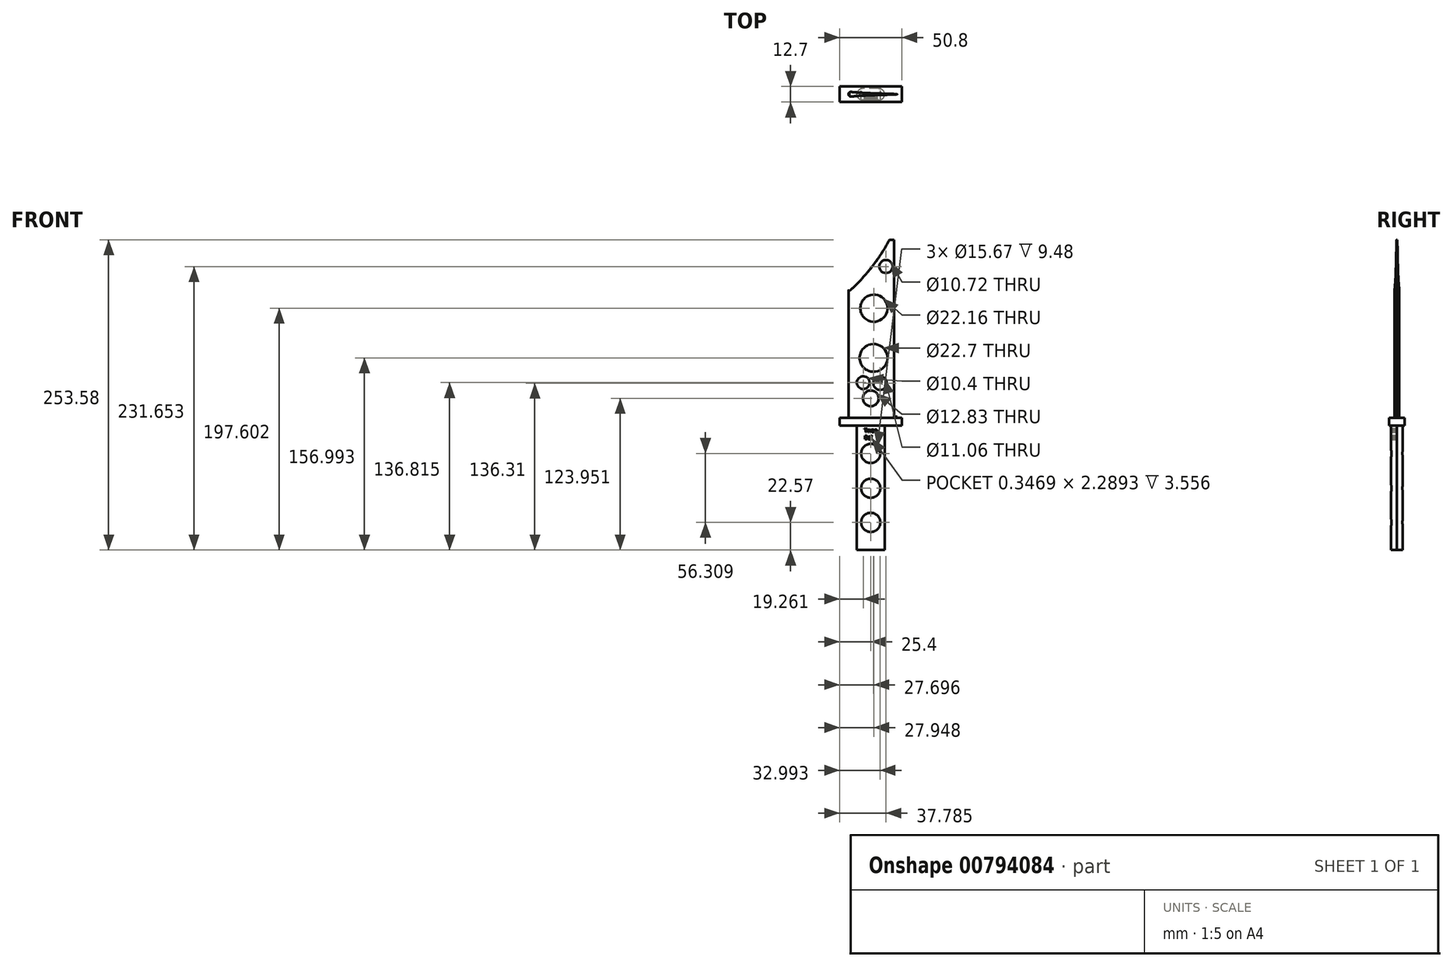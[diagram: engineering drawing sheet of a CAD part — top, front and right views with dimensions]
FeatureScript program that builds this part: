
annotation { "Feature Type Name" : "Feature", "Feature Type Description" : "" }
export const myFeature = defineFeature(function(context is Context, id is Id, definition is map)
    precondition{}
    {
        {
            var Q0;
            Q0=qCreatedBy(makeId("Top.planeOp"),FACE);
            var sketch = newSketch(context, id + "F0", { "sketchPlane" : qUnion([Q0])});
            skLineSegment(sketch, "E0.bottom", {"start": v(25.4, 6.35) * mm, "end": v(-25.4, 6.35) * mm});
            skLineSegment(sketch, "E0.top", {"start": v(25.4, -6.35) * mm, "end": v(-25.4, -6.35) * mm});
            skLineSegment(sketch, "E0.left", {"start": v(25.4, 6.35) * mm, "end": v(25.4, -6.35) * mm});
            skLineSegment(sketch, "E0.right", {"start": v(-25.4, 6.35) * mm, "end": v(-25.4, -6.35) * mm});
            skPoint(sketch, "E0.middle", {"position": v(0, 0) * mm});
            skSolve(sketch);
        }
        {
            var Q0;
            Q0=makeQuery(id+"F0.imprint","IMPRINT",FACE,{"disambiguationData":[TD([[makeQuery(id+"F0.imprint","IMPRINT",EDGE,{"derivedFrom":sQuery(id+"F0.wireOp",EDGE,"E0.bottom")}),1.0]])]});
            extrude(context, id + "F1", {"entities" : qUnion([Q0]), "depth" : 6.35 * mm, "offsetDistance" : 25.4 * mm});
        }
        {
            var Q0;
            Q0=makeQuery(id+"F1.opExtrude","CAP_FACE",FACE,{"disambiguationData":[OSD([sQuery(id+"F0.wireOp",EDGE,"E0.bottom"),sQuery(id+"F0.wireOp",EDGE,"E0.top"),sQuery(id+"F0.wireOp",EDGE,"E0.left"),sQuery(id+"F0.wireOp",EDGE,"E0.right")])],"isStart":true});
            var sketch = newSketch(context, id + "F2", { "sketchPlane" : qUnion([Q0])});
            skLineSegment(sketch, "E1.bottom", {"start": v(11.44, 4.74) * mm, "end": v(-11.44, 4.74) * mm});
            skLineSegment(sketch, "E1.top", {"start": v(11.44, -4.74) * mm, "end": v(-11.44, -4.74) * mm});
            skLineSegment(sketch, "E1.left", {"start": v(11.44, 4.74) * mm, "end": v(11.44, -4.74) * mm});
            skLineSegment(sketch, "E1.right", {"start": v(-11.44, 4.74) * mm, "end": v(-11.44, -4.74) * mm});
            skPoint(sketch, "E1.middle", {"position": v(0, 0) * mm});
            skSolve(sketch);
        }
        {
            var Q0;
            Q0=makeQuery(id+"F2.imprint","IMPRINT",FACE,{"disambiguationData":[TD([[makeQuery(id+"F2.imprint","IMPRINT",EDGE,{"derivedFrom":sQuery(id+"F2.wireOp",EDGE,"E1.bottom")}),1.0]])]});
            extrude(context, id + "F3", {"entities" : qUnion([Q0]), "operationType" : NewBodyOperationType.ADD, "depth" : 101.6 * mm, "offsetDistance" : 25.4 * mm});
        }
        {
            var Q0;
            Q0=makeQuery(id+"F1.opExtrude","CAP_FACE",FACE,{"disambiguationData":[OSD([sQuery(id+"F0.wireOp",EDGE,"E0.bottom"),sQuery(id+"F0.wireOp",EDGE,"E0.top"),sQuery(id+"F0.wireOp",EDGE,"E0.left"),sQuery(id+"F0.wireOp",EDGE,"E0.right")])],"isStart":false});
            var sketch = newSketch(context, id + "F4", { "sketchPlane" : qUnion([Q0])});
            skLineSegment(sketch, "E2", {"start": v(-25.4, 0) * mm, "end": v(25.4, 0) * mm});
            skSolve(sketch);
        }
        {
            var Q0;
            {var subQ0=sQuery(id+"F4.wireOp",EDGE,"E2");Q0=makeQuery(id+"F4.imprint","IMPRINT",FACE,{"disambiguationData":[TD([[makeQuery(id+"F4.imprint","IMPRINT",EDGE,{"derivedFrom":subQ0}),1.0]])]});}
            var sketch = newSketch(context, id + "F5", { "sketchPlane" : qUnion([Q0])});
            skLineSegment(sketch, "E3", {"start": v(-18.25, 2.1) * mm, "end": v(-18.25, 0) * mm});
            skLineSegment(sketch, "E4", {"start": v(-18.25, 0) * mm, "end": v(-18.25, -2.1) * mm});
            skLineSegment(sketch, "E5", {"start": v(-1.88, -0.92) * mm, "end": v(-1.88, 0) * mm});
            skLineSegment(sketch, "E6", {"start": v(-1.88, 0) * mm, "end": v(-1.88, 0.92) * mm});
            skFitSpline(sketch, "E7", {"points": [v(-18.25, -2.1) * mm, v(-1.88, -0.92) * mm, v(21.71, 0) * mm, v(-1.88, 0.92) * mm, v(-18.25, 2.1) * mm], "startDerivative": vector(56.8, 5.64) * mm, "endDerivative": vector(-56.8, 5.64) * mm});
            skSolve(sketch);
        }
        {
            var Q0;
            Q0=qSketchRegion(id+"F5",true);
            extrude(context, id + "F6", {"entities" : qUnion([Q0]), "operationType" : NewBodyOperationType.ADD, "depth" : 158.75 * mm, "offsetDistance" : 25.4 * mm});
        }
        {
            var Q0;
            Q0=makeQuery(id+"F6.opExtrude","SWEPT_EDGE",EDGE,{"disambiguationData":[OSD([sQuery(id+"F5.wireOp",EDGE,"E4"),sQuery(id+"F5.wireOp",EDGE,"E7")])]});
            fillet(context, id + "F7", {"entities" : qUnion([Q0]), "radius" : 2.07 * mm, "tangentPropagation" : true, "allowEdgeOverflow" : false});
        }
        {
            var Q0;
            Q0=makeQuery(id+"F6.opExtrude","SWEPT_EDGE",EDGE,{"disambiguationData":[OSD([sQuery(id+"F5.wireOp",EDGE,"E3"),sQuery(id+"F5.wireOp",EDGE,"E7")])]});
            fillet(context, id + "F8", {"entities" : qUnion([Q0]), "radius" : 1.87 * mm, "tangentPropagation" : true, "allowEdgeOverflow" : false});
        }
        {
            var Q0;
            Q0=makeQuery(id+"F3.opExtrude","SWEPT_EDGE",EDGE,{"disambiguationData":[OSD([sQuery(id+"F2.wireOp",EDGE,"E1.bottom"),sQuery(id+"F2.wireOp",EDGE,"E1.right")])]});
            var Q1;
            Q1=makeQuery(id+"F3.opExtrude","SWEPT_EDGE",EDGE,{"disambiguationData":[OSD([sQuery(id+"F2.wireOp",EDGE,"E1.top"),sQuery(id+"F2.wireOp",EDGE,"E1.right")])]});
            var Q2;
            Q2=makeQuery(id+"F3.opExtrude","SWEPT_EDGE",EDGE,{"disambiguationData":[OSD([sQuery(id+"F2.wireOp",EDGE,"E1.top"),sQuery(id+"F2.wireOp",EDGE,"E1.left")])]});
            var Q3;
            Q3=makeQuery(id+"F3.opExtrude","SWEPT_EDGE",EDGE,{"disambiguationData":[OSD([sQuery(id+"F2.wireOp",EDGE,"E1.bottom"),sQuery(id+"F2.wireOp",EDGE,"E1.left")])]});
            fillet(context, id + "F9", {"entities" : qUnion([Q0, Q1, Q2, Q3]), "radius" : 5.08 * mm, "tangentPropagation" : true, "allowEdgeOverflow" : false});
        }
        {
            var Q0;
            Q0=makeQuery(id+"F3.opExtrude","SWEPT_FACE",FACE,{"disambiguationData":[OSD([sQuery(id+"F2.wireOp",EDGE,"E1.top")])]});
            var sketch = newSketch(context, id + "F10", { "sketchPlane" : qUnion([Q0])});
            skPoint(sketch, "E8", {"position": v(0, -79.03) * mm});
            skPoint(sketch, "E9", {"position": v(0, -22.72) * mm});
            skPoint(sketch, "E10", {"position": v(0, -51.12) * mm});
            skSolve(sketch);
        }
        {
            var Q0;
            Q0=sQuery(id+"F10.wireOp",VERTEX,"E8");
            var Q1;
            Q1=sQuery(id+"F10.wireOp",VERTEX,"E10");
            var Q2;
            Q2=sQuery(id+"F10.wireOp",VERTEX,"E9");
            var Q3;
            Q3=makeQuery(id+"F1.opExtrude","SWEPT_BODY",BODY,{"disambiguationData":[OSD([sQuery(id+"F0.wireOp",EDGE,"E0.bottom"),sQuery(id+"F0.wireOp",EDGE,"E0.top"),sQuery(id+"F0.wireOp",EDGE,"E0.left"),sQuery(id+"F0.wireOp",EDGE,"E0.right")])]});
            hole(context, id + "F11", {"style" : HoleStyle.SIMPLE, "endStyle" : HoleEndStyle.BLIND, "holeDiameter" : 15.67 * mm, "majorDiameter" : 6.35 * mm, "holeDepth" : 10.16 * mm, "isTappedThrough" : true, "tappedDepth" : 12.7 * mm, "tapClearance" : 3, "locations" : qUnion([Q0, Q1, Q2]), "scope" : qUnion([Q3])});
        }
        {
            var Q0;
            {var subQ0=makeQuery(id+"F1.opExtrude","CAP_FACE",FACE,{"disambiguationData":[OSD([sQuery(id+"F0.wireOp",EDGE,"E0.bottom"),sQuery(id+"F0.wireOp",EDGE,"E0.top"),sQuery(id+"F0.wireOp",EDGE,"E0.left"),sQuery(id+"F0.wireOp",EDGE,"E0.right")])],"isStart":true});var subQ1=sQuery(id+"F2.wireOp",EDGE,"E1.bottom");Q0=makeQuery(id+"F11.hole-2.boolean.opBoolean","SPLIT",FACE,{"disambiguationData":[TD([subQ0])],"derivedFrom":makeQuery(id+"F11.hole-1.boolean.opBoolean","SPLIT",FACE,{"disambiguationData":[TD([subQ0])],"derivedFrom":makeQuery(id+"F11.hole-0.boolean.opBoolean","SPLIT",FACE,{"disambiguationData":[TD([subQ0])],"derivedFrom":makeQuery(id+"F3.opExtrude","SWEPT_FACE",FACE,{"disambiguationData":[OSD([subQ1])]})})})});}
            var sketch = newSketch(context, id + "F12", { "sketchPlane" : qUnion([Q0])});
            skText(sketch, "E11", { "text": "Twee \nBoi                                                                                                              ", "fontName": "OpenSans-Regular.ttf"});
            const initialGuessF12  = {"E11": [-0.00528, -0.00538, 1, 0, 0.00308]};
            skSetInitialGuess(sketch, initialGuessF12);
            skSolve(sketch);
        }
        {
            var Q0;
            Q0=qSketchRegion(id+"F12",true);
            extrude(context, id + "F13", {"entities" : qUnion([Q0]), "operationType" : NewBodyOperationType.REMOVE, "oppositeDirection" : true, "depth" : 3.56 * mm, "offsetDistance" : 25.4 * mm});
        }
        {
            var Q0;
            Q0=makeQuery(id+"F1.opExtrude","SWEPT_FACE",FACE,{"disambiguationData":[OSD([sQuery(id+"F0.wireOp",EDGE,"E0.bottom")])]});
            cPlane(context, id + "F14", {"entities" : qUnion([Q0]), "cplaneType" : CPlaneType.OFFSET, "offset" : 25 * mm, "width" : 150 * mm, "height" : 150 * mm});
        }
        {
            var Q0;
            Q0=qCreatedBy(id+"F14.planeOp",FACE);
            var sketch = newSketch(context, id + "F15", { "sketchPlane" : qUnion([Q0])});
            skArc(sketch, "E12", {"start": v(-21.51, 165.1) * mm, "mid": v(-5.05, 135.3) * mm, "end": v(17.6, 109.9) * mm});
            skLineSegment(sketch, "E13", {"start": v(-21.51, 165.1) * mm, "end": v(0, 176.98) * mm});
            skLineSegment(sketch, "E14", {"start": v(0, 176.98) * mm, "end": v(26.33, 177.16) * mm});
            skLineSegment(sketch, "E15", {"start": v(26.33, 177.16) * mm, "end": v(55.28, 158.8) * mm});
            skLineSegment(sketch, "E16", {"start": v(55.28, 158.8) * mm, "end": v(17.6, 109.9) * mm});
            skSolve(sketch);
        }
        {
            var Q0;
            Q0=makeQuery(id+"F15.imprint","IMPRINT",FACE,{"disambiguationData":[TD([[makeQuery(id+"F15.imprint","IMPRINT",EDGE,{"derivedFrom":sQuery(id+"F15.wireOp",EDGE,"E12")}),1.0]])]});
            extrude(context, id + "F16", {"entities" : qUnion([Q0]), "operationType" : NewBodyOperationType.REMOVE, "oppositeDirection" : true, "depth" : 42.1 * mm, "offsetDistance" : 25 * mm});
        }
        {
            var Q0;
            Q0=qCreatedBy(id+"F14.planeOp",FACE);
            var sketch = newSketch(context, id + "F17", { "sketchPlane" : qUnion([Q0])});
            skCircle(sketch, "E17", {"center": v(-2.55, 96) * mm, "radius": 11.08 * mm});
            skCircle(sketch, "E18", {"center": v(-12.38, 130.05) * mm, "radius": 5.36 * mm});
            skCircle(sketch, "E19", {"center": v(-2.3, 55.4) * mm, "radius": 11.35 * mm});
            skCircle(sketch, "E20", {"center": v(-7.6, 34.71) * mm, "radius": 5.53 * mm});
            skCircle(sketch, "E21", {"center": v(6.14, 35.21) * mm, "radius": 5.2 * mm});
            skCircle(sketch, "E22", {"center": v(0, 22.35) * mm, "radius": 6.41 * mm});
            skSolve(sketch);
        }
        {
            var Q0;
            Q0=makeQuery(id+"F17.imprint","IMPRINT",FACE,{"disambiguationData":[TD([[makeQuery(id+"F17.imprint","IMPRINT",EDGE,{"derivedFrom":sQuery(id+"F17.wireOp",EDGE,"E18")}),1.0]])]});
            extrude(context, id + "F18", {"entities" : qUnion([Q0]), "operationType" : NewBodyOperationType.REMOVE, "oppositeDirection" : true, "depth" : 43 * mm, "offsetDistance" : 25 * mm});
        }
        {
            var Q0;
            Q0=makeQuery(id+"F17.imprint","IMPRINT",FACE,{"disambiguationData":[TD([[makeQuery(id+"F17.imprint","IMPRINT",EDGE,{"derivedFrom":sQuery(id+"F17.wireOp",EDGE,"E17")}),1.0]])]});
            extrude(context, id + "F19", {"entities" : qUnion([Q0]), "operationType" : NewBodyOperationType.REMOVE, "oppositeDirection" : true, "depth" : 49 * mm, "offsetDistance" : 25 * mm});
        }
        {
            var Q0;
            Q0=makeQuery(id+"F17.imprint","IMPRINT",FACE,{"disambiguationData":[TD([[makeQuery(id+"F17.imprint","IMPRINT",EDGE,{"derivedFrom":sQuery(id+"F17.wireOp",EDGE,"E19")}),1.0]])]});
            extrude(context, id + "F20", {"entities" : qUnion([Q0]), "operationType" : NewBodyOperationType.REMOVE, "oppositeDirection" : true, "depth" : 52 * mm, "offsetDistance" : 25 * mm});
        }
        {
            var Q0;
            Q0=makeQuery(id+"F17.imprint","IMPRINT",FACE,{"disambiguationData":[TD([[makeQuery(id+"F17.imprint","IMPRINT",EDGE,{"derivedFrom":sQuery(id+"F17.wireOp",EDGE,"E20")}),1.0]])]});
            var Q1;
            Q1=makeQuery(id+"F17.imprint","IMPRINT",FACE,{"disambiguationData":[TD([[makeQuery(id+"F17.imprint","IMPRINT",EDGE,{"derivedFrom":sQuery(id+"F17.wireOp",EDGE,"E21")}),1.0]])]});
            var Q2;
            Q2=makeQuery(id+"F17.imprint","IMPRINT",FACE,{"disambiguationData":[TD([[makeQuery(id+"F17.imprint","IMPRINT",EDGE,{"derivedFrom":sQuery(id+"F17.wireOp",EDGE,"E22")}),1.0]])]});
            extrude(context, id + "F21", {"entities" : qUnion([Q0, Q1, Q2]), "operationType" : NewBodyOperationType.REMOVE, "oppositeDirection" : true, "depth" : 45 * mm, "offsetDistance" : 25 * mm});
        }
        {
            var Q0;
            Q0=qCreatedBy(id+"F14.planeOp",FACE);
            var sketch = newSketch(context, id + "F22", { "sketchPlane" : qUnion([Q0])});
            skLineSegment(sketch, "E23", {"start": v(-19.19, 167.42) * mm, "end": v(-19.19, 7.45) * mm});
            skLineSegment(sketch, "E24", {"start": v(-19.19, 7.45) * mm, "end": v(-33.65, 7.45) * mm});
            skLineSegment(sketch, "E25", {"start": v(-33.65, 7.45) * mm, "end": v(-28.53, 163.8) * mm});
            skLineSegment(sketch, "E26", {"start": v(-28.53, 163.8) * mm, "end": v(-19.19, 167.42) * mm});
            skSolve(sketch);
        }
        {
            var Q0;
            Q0=makeQuery(id+"F22.imprint","IMPRINT",FACE,{"disambiguationData":[TD([[makeQuery(id+"F22.imprint","IMPRINT",EDGE,{"derivedFrom":sQuery(id+"F22.wireOp",EDGE,"E23")}),-1.0]])]});
            extrude(context, id + "F23", {"entities" : qUnion([Q0]), "operationType" : NewBodyOperationType.REMOVE, "oppositeDirection" : true, "depth" : 40.4 * mm, "offsetDistance" : 25 * mm});
        }
        {
            var Q0;
            Q0=qCreatedBy(id+"F14.planeOp",FACE);
            var sketch = newSketch(context, id + "F24", { "sketchPlane" : qUnion([Q0])});
            skLineSegment(sketch, "E27", {"start": v(-28.65, 151.98) * mm, "end": v(-8.03, 151.98) * mm});
            skLineSegment(sketch, "E28", {"start": v(-8.03, 151.98) * mm, "end": v(-13.94, 180.63) * mm});
            skLineSegment(sketch, "E29", {"start": v(-13.94, 180.63) * mm, "end": v(-30.37, 177.23) * mm});
            skLineSegment(sketch, "E30", {"start": v(-30.37, 177.23) * mm, "end": v(-28.65, 151.98) * mm});
            skSolve(sketch);
        }
        {
            var Q0;
            Q0=makeQuery(id+"F24.imprint","IMPRINT",FACE,{"disambiguationData":[TD([[makeQuery(id+"F24.imprint","IMPRINT",EDGE,{"derivedFrom":sQuery(id+"F24.wireOp",EDGE,"E27")}),1.0]])]});
            extrude(context, id + "F25", {"entities" : qUnion([Q0]), "operationType" : NewBodyOperationType.REMOVE, "oppositeDirection" : true, "depth" : 52.1 * mm, "offsetDistance" : 25 * mm});
        }
    });
